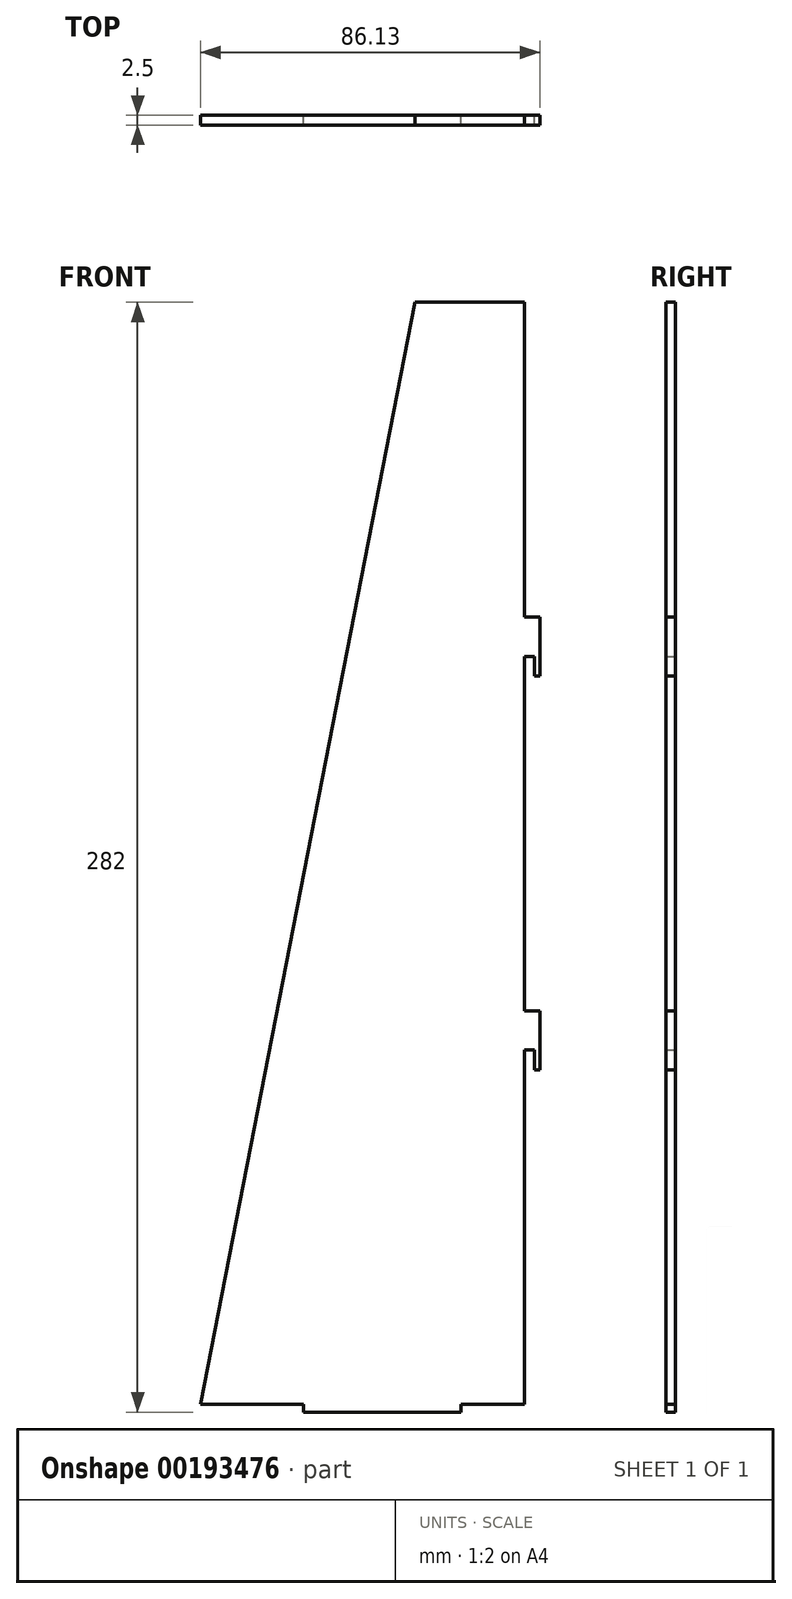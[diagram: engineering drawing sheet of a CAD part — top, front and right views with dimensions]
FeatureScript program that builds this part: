
annotation { "Feature Type Name" : "Feature", "Feature Type Description" : "" }
export const myFeature = defineFeature(function(context is Context, id is Id, definition is map)
    precondition{}
    {
        {
            var Q0;
            Q0=qCreatedBy(makeId("Front.planeOp"),FACE);
            var sketch = newSketch(context, id + "F0", { "sketchPlane" : qUnion([Q0])});
            skLineSegment(sketch, "E0", {"start": v(-86.13, 0) * mm, "end": v(-31.7, 280) * mm});
            skLineSegment(sketch, "E1", {"start": v(-31.7, 280) * mm, "end": v(0, 280) * mm});
            skLineSegment(sketch, "E2", {"start": v(0, 280) * mm, "end": v(0, 0) * mm});
            skLineSegment(sketch, "E3", {"start": v(0, 0) * mm, "end": v(-20, 0) * mm});
            skLineSegment(sketch, "E4", {"start": v(-60, 0) * mm, "end": v(-60, -2) * mm});
            skLineSegment(sketch, "E5", {"start": v(-60, -2) * mm, "end": v(-20, -2) * mm});
            skLineSegment(sketch, "E6", {"start": v(-20, -2) * mm, "end": v(-20, 0) * mm});
            skLineSegment(sketch, "E7.trimOffspring", {"start": v(-60, 0) * mm, "end": v(-86.13, 0) * mm});
            skSolve(sketch);
        }
        {
            var Q0;
            Q0 = qSketchRegion(id + "F0", true);
            extrude(context, id + "F1", {"entities" : qUnion([Q0]), "depth" : 2.5 * mm});
        }
        {
            var Q0;
            Q0=qCreatedBy(makeId("Front.planeOp"),FACE);
            var sketch = newSketch(context, id + "F2", { "sketchPlane" : qUnion([Q0])});
            skLineSegment(sketch, "E8", {"start": v(25.52, 285.47) * mm, "end": v(-3.88, 285.47) * mm});
            skLineSegment(sketch, "E9", {"start": v(-3.88, 285.47) * mm, "end": v(-3.88, 200) * mm});
            skLineSegment(sketch, "E10", {"start": v(-3.88, 200) * mm, "end": v(3.67, 200) * mm});
            skLineSegment(sketch, "E11", {"start": v(3.67, 200) * mm, "end": v(3.67, 185) * mm});
            skLineSegment(sketch, "E12", {"start": v(3.67, 185) * mm, "end": v(-1.33, 185) * mm});
            skLineSegment(sketch, "E13", {"start": v(-1.33, 185) * mm, "end": v(-1.33, 190) * mm});
            skLineSegment(sketch, "E14", {"start": v(-1.33, 190) * mm, "end": v(-3.88, 190) * mm});
            skLineSegment(sketch, "E15", {"start": v(-3.88, 190) * mm, "end": v(-3.88, 100) * mm});
            skLineSegment(sketch, "E16.0.1.0", {"start": v(3.67, 100) * mm, "end": v(3.67, 85) * mm});
            skLineSegment(sketch, "E16.0.1.1", {"start": v(-3.88, 100) * mm, "end": v(3.67, 100) * mm});
            skLineSegment(sketch, "E16.0.1.2", {"start": v(3.67, 85) * mm, "end": v(-1.33, 85) * mm});
            skLineSegment(sketch, "E16.0.1.3", {"start": v(-1.33, 85) * mm, "end": v(-1.33, 90) * mm});
            skLineSegment(sketch, "E16.0.1.4", {"start": v(-1.33, 90) * mm, "end": v(-3.88, 90) * mm});
            skLineSegment(sketch, "E16.0.1.5", {"start": v(-3.88, 90) * mm, "end": v(-3.88, 0) * mm});
            skLineSegment(sketch, "E16.direction1", {"start": v(-1.33, 185) * mm, "end": v(23.67, 185) * mm, "construction": true});
            skLineSegment(sketch, "E16.direction2", {"start": v(-1.33, 185) * mm, "end": v(-1.33, 85) * mm, "construction": true});
            skLineSegment(sketch, "E17", {"start": v(-3.88, 0) * mm, "end": v(25.52, 0) * mm});
            skLineSegment(sketch, "E18", {"start": v(25.52, 0) * mm, "end": v(25.52, 285.47) * mm});
            skSolve(sketch);
        }
        {
            var Q0;
            Q0 = qSketchRegion(id + "F2", true);
            extrude(context, id + "F3", {"entities" : qUnion([Q0]), "operationType" : NewBodyOperationType.REMOVE, "depth" : 25 * mm});
        }
    });
